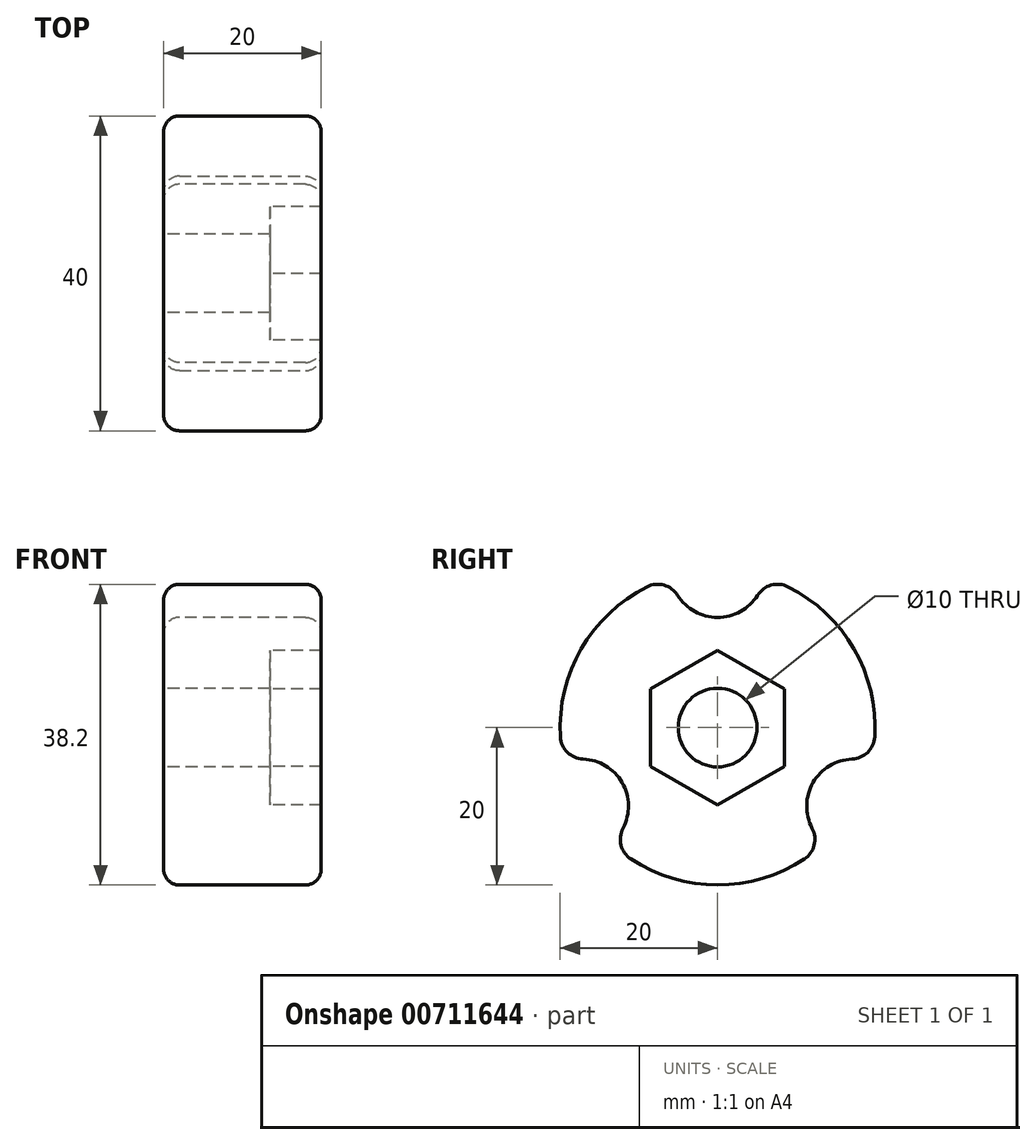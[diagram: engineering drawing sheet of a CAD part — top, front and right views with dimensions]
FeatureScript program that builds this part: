
annotation { "Feature Type Name" : "Feature", "Feature Type Description" : "" }
export const myFeature = defineFeature(function(context is Context, id is Id, definition is map)
    precondition{}
    {
        {
            var Q0;
            Q0=qCreatedBy(makeId("Right.planeOp"),FACE);
            var sketch = newSketch(context, id + "F0", { "sketchPlane" : qUnion([Q0])});
            skCircle(sketch, "E0", {"center": v(0, 0) * mm, "radius": 20 * mm});
            skCircle(sketch, "E1", {"center": v(0, 20) * mm, "radius": 6 * mm});
            skCircle(sketch, "E2.1.0", {"center": v(-17.32, -10) * mm, "radius": 6 * mm});
            skCircle(sketch, "E2.2.0", {"center": v(17.32, -10) * mm, "radius": 6 * mm});
            skCircle(sketch, "E3.cCircle", {"center": v(0, 0) * mm, "radius": 8.5 * mm, "construction": true});
            skLineSegment(sketch, "E3.0", {"start": v(0, 9.81) * mm, "end": v(8.5, 4.9) * mm});
            skLineSegment(sketch, "E3.1", {"start": v(8.5, 4.9) * mm, "end": v(8.5, -4.9) * mm});
            skLineSegment(sketch, "E3.2", {"start": v(8.5, -4.9) * mm, "end": v(0, -9.81) * mm});
            skLineSegment(sketch, "E3.3", {"start": v(0, -9.81) * mm, "end": v(-8.5, -4.9) * mm});
            skLineSegment(sketch, "E3.4", {"start": v(-8.5, -4.9) * mm, "end": v(-8.5, 4.9) * mm});
            skLineSegment(sketch, "E3.5", {"start": v(-8.5, 4.9) * mm, "end": v(0, 9.81) * mm});
            skPoint(sketch, "E3.0.midPoint", {"position": v(4.25, 7.36) * mm});
            skCircle(sketch, "E4", {"center": v(0, 0) * mm, "radius": 5 * mm});
            skSolve(sketch);
        }
        {
            var Q0;
            Q0=makeQuery(id+"F0.imprint","IMPRINT",FACE,{"disambiguationData":[TD([[makeQuery(id+"F0.imprint","IMPRINT",EDGE,{"derivedFrom":sQuery(id+"F0.wireOp",EDGE,"E3.0")}),1.0]])]});
            extrude(context, id + "F1", {"entities" : qUnion([Q0]), "depth" : 20 * mm, "offsetDistance" : 25.4 * mm});
        }
        {
            var Q0;
            Q0=makeQuery(id+"F0.imprint","IMPRINT",FACE,{"disambiguationData":[TD([[makeQuery(id+"F0.imprint","IMPRINT",EDGE,{"derivedFrom":sQuery(id+"F0.wireOp",EDGE,"E3.0")}),-1.0]])]});
            extrude(context, id + "F2", {"entities" : qUnion([Q0]), "operationType" : NewBodyOperationType.ADD, "depth" : 13.5 * mm, "offsetDistance" : 25.4 * mm});
        }
        {
            var Q0;
            {var subQ0=sQuery(id+"F0.wireOp",EDGE,"E2.1.0");var subQ1=sQuery(id+"F0.wireOp",EDGE,"E0");Q0=makeQuery(id+"F1.opExtrude","SWEPT_EDGE",EDGE,{"disambiguationData":[OSD([subQ1,subQ0]),TDD([makeQuery(id+"F0.imprint","INTERSECT",VERTEX,{"disambiguationData":[OD(0.0)],"derivedFrom":[subQ1,subQ0]})])]});}
            var Q1;
            {var subQ0=sQuery(id+"F0.wireOp",EDGE,"E2.1.0");var subQ1=sQuery(id+"F0.wireOp",EDGE,"E0");Q1=makeQuery(id+"F1.opExtrude","SWEPT_EDGE",EDGE,{"disambiguationData":[OSD([subQ1,subQ0]),TDD([makeQuery(id+"F0.imprint","INTERSECT",VERTEX,{"disambiguationData":[OD(1.0)],"derivedFrom":[subQ1,subQ0]})])]});}
            var Q2;
            {var subQ0=sQuery(id+"F0.wireOp",EDGE,"E1");var subQ1=sQuery(id+"F0.wireOp",EDGE,"E0");Q2=makeQuery(id+"F1.opExtrude","SWEPT_EDGE",EDGE,{"disambiguationData":[OSD([subQ1,subQ0]),TDD([makeQuery(id+"F0.imprint","INTERSECT",VERTEX,{"disambiguationData":[OD(1.0)],"derivedFrom":[subQ1,subQ0]})])]});}
            var Q3;
            {var subQ0=sQuery(id+"F0.wireOp",EDGE,"E1");var subQ1=sQuery(id+"F0.wireOp",EDGE,"E0");Q3=makeQuery(id+"F1.opExtrude","SWEPT_EDGE",EDGE,{"disambiguationData":[OSD([subQ1,subQ0]),TDD([makeQuery(id+"F0.imprint","INTERSECT",VERTEX,{"disambiguationData":[OD(0.0)],"derivedFrom":[subQ1,subQ0]})])]});}
            var Q4;
            {var subQ0=sQuery(id+"F0.wireOp",EDGE,"E2.2.0");var subQ1=sQuery(id+"F0.wireOp",EDGE,"E0");Q4=makeQuery(id+"F1.opExtrude","SWEPT_EDGE",EDGE,{"disambiguationData":[OSD([subQ1,subQ0]),TDD([makeQuery(id+"F0.imprint","INTERSECT",VERTEX,{"disambiguationData":[OD(1.0)],"derivedFrom":[subQ1,subQ0]})])]});}
            var Q5;
            {var subQ0=sQuery(id+"F0.wireOp",EDGE,"E2.2.0");var subQ1=sQuery(id+"F0.wireOp",EDGE,"E0");Q5=makeQuery(id+"F1.opExtrude","SWEPT_EDGE",EDGE,{"disambiguationData":[OSD([subQ1,subQ0]),TDD([makeQuery(id+"F0.imprint","INTERSECT",VERTEX,{"disambiguationData":[OD(0.0)],"derivedFrom":[subQ1,subQ0]})])]});}
            fillet(context, id + "F3", {"entities" : qUnion([Q0, Q1, Q2, Q3, Q4, Q5]), "radius" : 3 * mm, "tangentPropagation" : true, "allowEdgeOverflow" : false});
        }
        {
            var Q0;
            {var subQ0=sQuery(id+"F0.wireOp",EDGE,"E0");Q0=makeQuery(id+"F1.opExtrude","CAP_EDGE",EDGE,{"disambiguationData":[OSD([subQ0]),TDD([makeQuery(id+"F0.imprint","IMPRINT",EDGE,{"disambiguationData":[TD([[makeQuery(id+"F0.imprint","INTERSECT",VERTEX,{"disambiguationData":[OD(1.0)],"derivedFrom":[subQ0,sQuery(id+"F0.wireOp",EDGE,"E2.1.0")]}),-1.0]])],"derivedFrom":subQ0})])],"isStart":false});}
            var Q1;
            Q1=makeQuery(id+"F1.opExtrude","CAP_EDGE",EDGE,{"disambiguationData":[OSD([sQuery(id+"F0.wireOp",EDGE,"E1")])],"isStart":true});
            fillet(context, id + "F4", {"entities" : qUnion([Q0, Q1]), "radius" : 2 * mm, "tangentPropagation" : true, "allowEdgeOverflow" : false});
        }
    });
